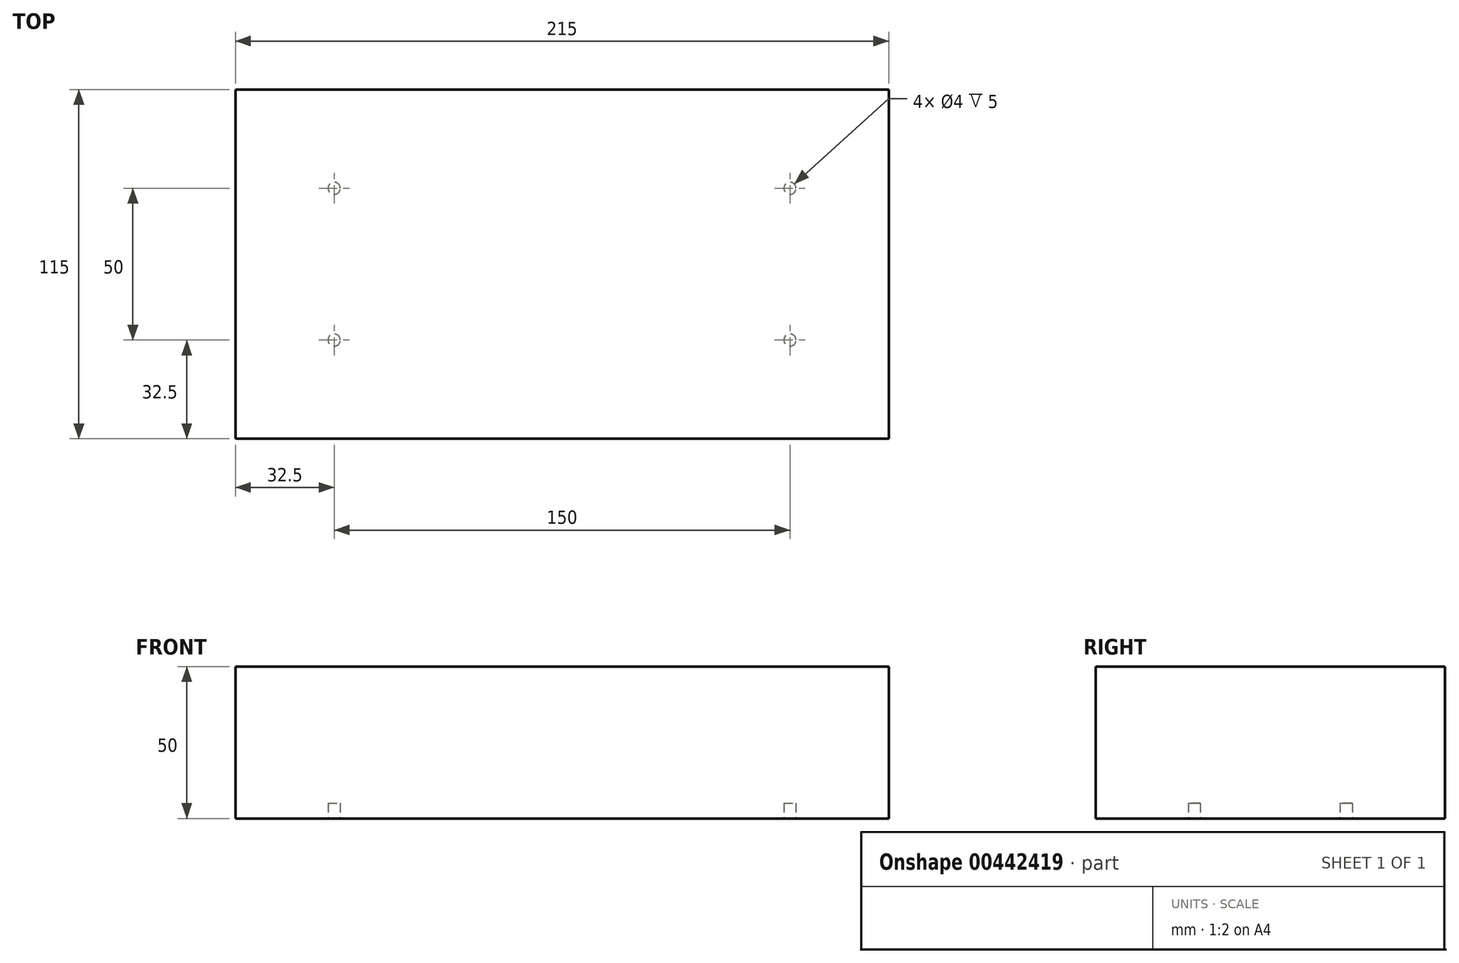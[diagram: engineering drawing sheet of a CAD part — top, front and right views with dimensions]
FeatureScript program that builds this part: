
annotation { "Feature Type Name" : "Feature", "Feature Type Description" : "" }
export const myFeature = defineFeature(function(context is Context, id is Id, definition is map)
    precondition{}
    {
        {
            var Q0;
            Q0=qCreatedBy(makeId("Top.planeOp"),FACE);
            var sketch = newSketch(context, id + "F0", { "sketchPlane" : qUnion([Q0])});
            skLineSegment(sketch, "E0.bottom", {"start": v(107.5, 57.5) * mm, "end": v(-107.5, 57.5) * mm});
            skLineSegment(sketch, "E0.top", {"start": v(107.5, -57.5) * mm, "end": v(-107.5, -57.5) * mm});
            skLineSegment(sketch, "E0.left", {"start": v(107.5, 57.5) * mm, "end": v(107.5, -57.5) * mm});
            skLineSegment(sketch, "E0.right", {"start": v(-107.5, 57.5) * mm, "end": v(-107.5, -57.5) * mm});
            skPoint(sketch, "E0.middle", {"position": v(0, 0) * mm});
            skSolve(sketch);
        }
        {
            var Q0;
            Q0 = qSketchRegion(id + "F0", true);
            extrude(context, id + "F1", {"entities" : qUnion([Q0]), "depth" : 50 * mm});
        }
        {
            var Q0;
            Q0=makeQuery(id+"F1.opExtrude","CAP_FACE",FACE,{"disambiguationData":[OSD([sQuery(id+"F0.wireOp",EDGE,"E0.bottom"),sQuery(id+"F0.wireOp",EDGE,"E0.top"),sQuery(id+"F0.wireOp",EDGE,"E0.left"),sQuery(id+"F0.wireOp",EDGE,"E0.right")])],"isStart":true});
            var sketch = newSketch(context, id + "F2", { "sketchPlane" : qUnion([Q0])});
            skCircle(sketch, "E1", {"center": v(-75, 25) * mm, "radius": 2 * mm});
            skCircle(sketch, "E2.0.1.0", {"center": v(-75, -25) * mm, "radius": 2 * mm});
            skCircle(sketch, "E2.1.0.0", {"center": v(75, 25) * mm, "radius": 2 * mm});
            skCircle(sketch, "E2.1.1.0", {"center": v(75, -25) * mm, "radius": 2 * mm});
            skLineSegment(sketch, "E2.direction1", {"start": v(-75, 25) * mm, "end": v(75, 25) * mm, "construction": true});
            skLineSegment(sketch, "E2.direction2", {"start": v(-75, 25) * mm, "end": v(-75, -25) * mm, "construction": true});
            skSolve(sketch);
        }
        {
            var Q0;
            Q0 = qSketchRegion(id + "F2", true);
            extrude(context, id + "F3", {"entities" : qUnion([Q0]), "operationType" : NewBodyOperationType.REMOVE, "oppositeDirection" : true, "depth" : 5 * mm});
        }
    });
